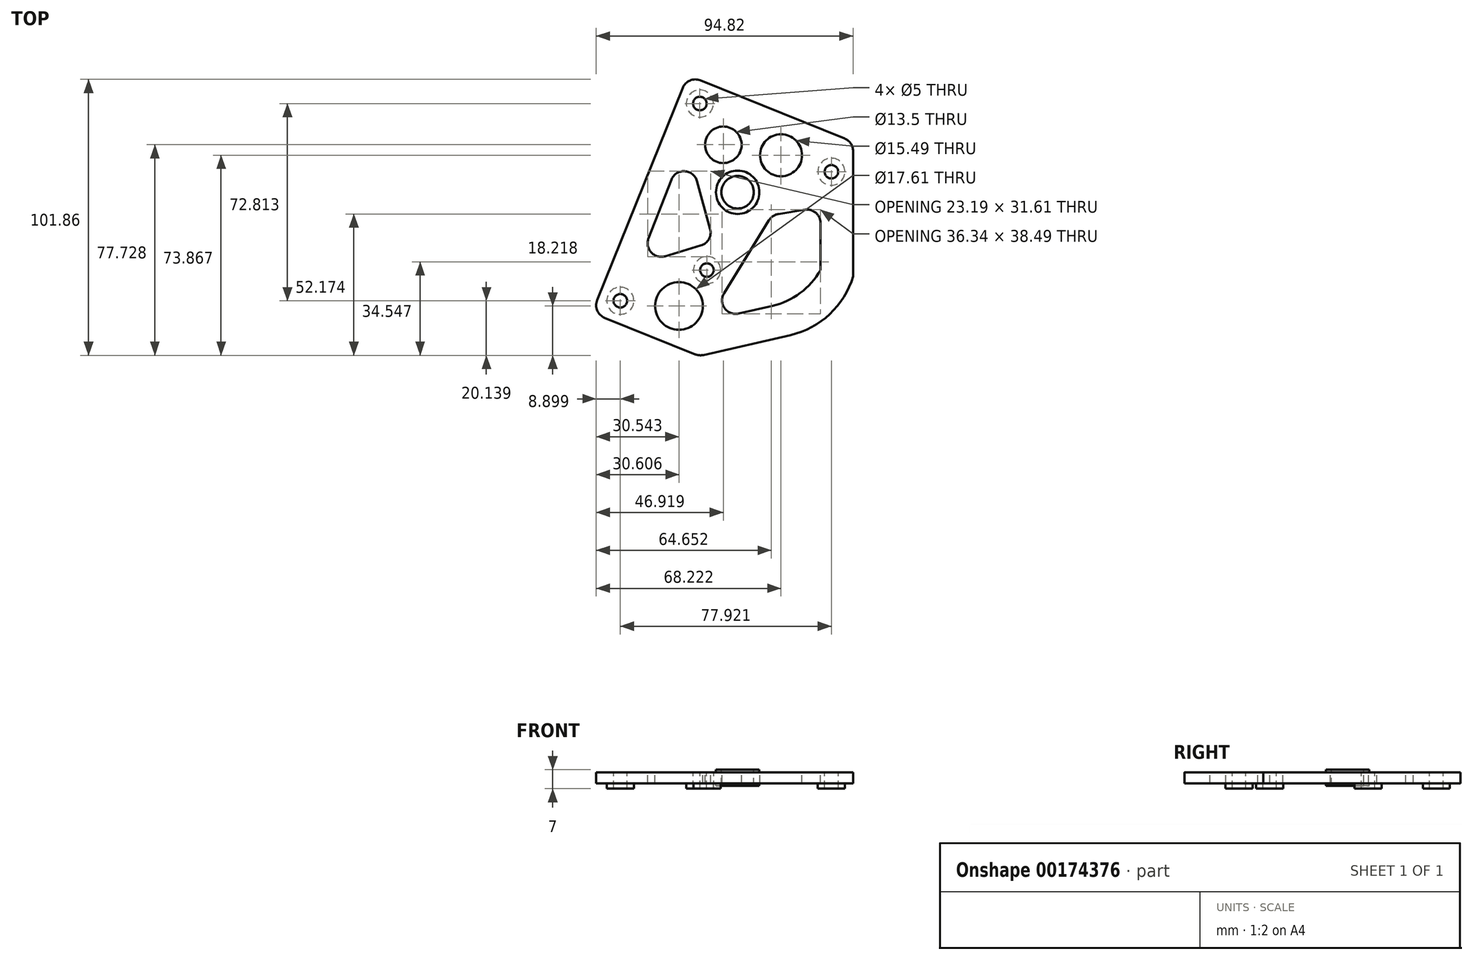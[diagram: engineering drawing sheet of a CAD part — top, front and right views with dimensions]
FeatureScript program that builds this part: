
annotation { "Feature Type Name" : "Feature", "Feature Type Description" : "" }
export const myFeature = defineFeature(function(context is Context, id is Id, definition is map)
    precondition{}
    {
        {
            var Q0;
            Q0=qCreatedBy(makeId("Top.planeOp"),FACE);
            var sketch = newSketch(context, id + "F0", { "sketchPlane" : qUnion([Q0])});
            skCircle(sketch, "E0", {"center": v(0, 0) * mm, "radius": 18.9 * mm});
            skCircle(sketch, "E1", {"center": v(0, 0) * mm, "radius": 20.4 * mm});
            skCircle(sketch, "E2", {"center": v(-30.9, 0) * mm, "radius": 2.5 * mm});
            skCircle(sketch, "E3", {"center": v(0, 0) * mm, "radius": 5.6 * mm, "construction": true});
            skCircle(sketch, "E4", {"center": v(-30.9, 0) * mm, "radius": 24.8 * mm, "construction": true});
            skCircle(sketch, "E5", {"center": v(-30.9, 0) * mm, "radius": 5.6 * mm, "construction": true});
            skCircle(sketch, "E6", {"center": v(-19.54, 28.74) * mm, "radius": 24.8 * mm, "construction": true});
            skCircle(sketch, "E7", {"center": v(-19.54, 28.74) * mm, "radius": 6 * mm});
            skLineSegment(sketch, "E8", {"start": v(-73.27, -15.75) * mm, "end": v(-37.94, 71.9) * mm});
            skLineSegment(sketch, "E9", {"start": v(-37.94, 71.9) * mm, "end": v(23.06, 47.31) * mm});
            skLineSegment(sketch, "E10", {"start": v(23.06, 47.31) * mm, "end": v(23.06, -2.33) * mm});
            skLineSegment(sketch, "E11", {"start": v(-73.27, -15.75) * mm, "end": v(-33.74, -31.69) * mm});
            skLineSegment(sketch, "E12", {"start": v(-33.74, -31.69) * mm, "end": v(0, -23.97) * mm});
            skArc(sketch, "E13", {"start": v(0, -23.97) * mm, "mid": v(14.46, -16.27) * mm, "end": v(23.06, -2.33) * mm});
            skLineSegment(sketch, "E14", {"start": v(0, 0) * mm, "end": v(9.83, 20.34) * mm, "construction": true});
            skLineSegment(sketch, "E15", {"start": v(9.83, 20.34) * mm, "end": v(-10.98, -23.06) * mm, "construction": true});
            skCircle(sketch, "E16", {"center": v(-19.54, 28.74) * mm, "radius": 8 * mm});
            skSolve(sketch);
        }
        {
            var Q0;
            Q0=makeQuery(id+"F0.imprint","IMPRINT",FACE,{"disambiguationData":[TD([[makeQuery(id+"F0.imprint","IMPRINT",EDGE,{"derivedFrom":sQuery(id+"F0.wireOp",EDGE,"E0")}),-1.0]])]});
            extrude(context, id + "F1", {"entities" : qUnion([Q0]), "oppositeDirection" : true, "depth" : 4 * mm});
        }
        {
            var Q0;
            Q0=qSketchRegion(id+"F0",true);
            extrude(context, id + "F2", {"entities" : qUnion([Q0]), "operationType" : NewBodyOperationType.ADD, "oppositeDirection" : true, "depth" : 4 * mm});
        }
        {
            var Q0;
            Q0=makeQuery(id+"F0.imprint","IMPRINT",FACE,{"disambiguationData":[TD([[makeQuery(id+"F0.imprint","IMPRINT",EDGE,{"derivedFrom":sQuery(id+"F0.wireOp",EDGE,"E0")}),1.0]])]});
            extrude(context, id + "F3", {"entities" : qUnion([Q0]), "operationType" : NewBodyOperationType.ADD, "oppositeDirection" : true, "depth" : 4 * mm});
        }
        {
            var Q0;
            Q0=makeQuery(id+"F0.imprint","IMPRINT",FACE,{"disambiguationData":[TD([[makeQuery(id+"F0.imprint","IMPRINT",EDGE,{"derivedFrom":sQuery(id+"F0.wireOp",EDGE,"E1")}),-1.0]])]});
            var sketch = newSketch(context, id + "F4", { "sketchPlane" : qUnion([Q0])});
            skCircle(sketch, "E17", {"center": v(-30.82, 0) * mm, "radius": 5 * mm});
            skCircle(sketch, "E18", {"center": v(-19.57, 28.75) * mm, "radius": 6 * mm});
            skCircle(sketch, "E19", {"center": v(15.06, 36.31) * mm, "radius": 5 * mm});
            skCircle(sketch, "E20", {"center": v(15.06, 36.31) * mm, "radius": 1.5 * mm});
            skCircle(sketch, "E21", {"center": v(-33.5, 61.5) * mm, "radius": 5 * mm});
            skCircle(sketch, "E22", {"center": v(-33.5, 61.5) * mm, "radius": 1.5 * mm});
            skCircle(sketch, "E23", {"center": v(-62.86, -11.32) * mm, "radius": 5 * mm});
            skCircle(sketch, "E24", {"center": v(-62.86, -11.32) * mm, "radius": 1.5 * mm});
            skLineSegment(sketch, "E25", {"start": v(-44.04, 33.33) * mm, "end": v(-52.43, 11.72) * mm});
            skLineSegment(sketch, "E26", {"start": v(-46.34, 5.12) * mm, "end": v(-33.12, 9.06) * mm});
            skLineSegment(sketch, "E27", {"start": v(-29.72, 15.17) * mm, "end": v(-34.55, 32.84) * mm});
            skLineSegment(sketch, "E28", {"start": v(-4.52, 20.7) * mm, "end": v(5.27, 22.28) * mm});
            skLineSegment(sketch, "E29", {"start": v(11.06, 17.34) * mm, "end": v(11.06, 0) * mm});
            skLineSegment(sketch, "E30", {"start": v(-7.98, 18.39) * mm, "end": v(-24.54, -8.55) * mm});
            skLineSegment(sketch, "E31", {"start": v(-19.16, -16.04) * mm, "end": v(-6.78, -13.2) * mm});
            skArc(sketch, "E32", {"start": v(-6.78, -13.2) * mm, "mid": v(3.52, -8.47) * mm, "end": v(11.06, 0) * mm});
            skPoint(sketch, "E33.visualSharp", {"position": v(-28.43, 10.46) * mm});
            skArc(sketch, "E33.filletArc", {"start": v(-33.12, 9.06) * mm, "mid": v(-30.17, 11.42) * mm, "end": v(-29.72, 15.17) * mm});
            skPoint(sketch, "E34.visualSharp", {"position": v(-38.55, 47.47) * mm});
            skArc(sketch, "E34.filletArc", {"start": v(-34.55, 32.84) * mm, "mid": v(-39.12, 36.52) * mm, "end": v(-44.04, 33.33) * mm});
            skPoint(sketch, "E35.visualSharp", {"position": v(-56.13, 2.2) * mm});
            skArc(sketch, "E35.filletArc", {"start": v(-52.43, 11.72) * mm, "mid": v(-51.44, 6.52) * mm, "end": v(-46.34, 5.12) * mm});
            skPoint(sketch, "E36.visualSharp", {"position": v(-30.78, -18.7) * mm});
            skArc(sketch, "E36.filletArc", {"start": v(-24.54, -8.55) * mm, "mid": v(-24.34, -14.08) * mm, "end": v(-19.16, -16.04) * mm});
            skPoint(sketch, "E37.visualSharp", {"position": v(11.06, 23.2) * mm});
            skArc(sketch, "E37.filletArc", {"start": v(11.06, 17.34) * mm, "mid": v(9.3, 21.14) * mm, "end": v(5.27, 22.28) * mm});
            skPoint(sketch, "E38.visualSharp", {"position": v(-6.78, 20.34) * mm});
            skArc(sketch, "E38.filletArc", {"start": v(-4.52, 20.7) * mm, "mid": v(-6.5, 19.92) * mm, "end": v(-7.98, 18.39) * mm});
            skCircle(sketch, "E39", {"center": v(-41.22, -13.24) * mm, "radius": 8.8 * mm});
            skCircle(sketch, "E40", {"center": v(-3.54, 42.4) * mm, "radius": 7.75 * mm});
            skCircle(sketch, "E41", {"center": v(-24.84, 46.27) * mm, "radius": 6.75 * mm});
            skSolve(sketch);
        }
        {
            var Q0;
            Q0=makeQuery(id+"F4.imprint","IMPRINT",FACE,{"disambiguationData":[TD([[makeQuery(id+"F4.imprint","IMPRINT",EDGE,{"derivedFrom":sQuery(id+"F4.wireOp",EDGE,"E17")}),1.0]])]});
            var Q1;
            Q1=sQuery(id+"F4.wireOp",EDGE,"E17");
            extrude(context, id + "F5", {"entities" : qUnion([Q0]), "operationType" : NewBodyOperationType.ADD, "surfaceEntities" : qUnion([Q1]), "oppositeDirection" : true, "depth" : 6 * mm});
        }
        {
            var Q0;
            Q0=makeQuery(id+"F4.imprint","IMPRINT",FACE,{"disambiguationData":[TD([[makeQuery(id+"F4.imprint","IMPRINT",EDGE,{"derivedFrom":sQuery(id+"F4.wireOp",EDGE,"E19")}),1.0]])]});
            var Q1;
            Q1=makeQuery(id+"F4.imprint","IMPRINT",FACE,{"disambiguationData":[TD([[makeQuery(id+"F4.imprint","IMPRINT",EDGE,{"derivedFrom":sQuery(id+"F4.wireOp",EDGE,"E21")}),1.0]])]});
            var Q2;
            Q2=makeQuery(id+"F4.imprint","IMPRINT",FACE,{"disambiguationData":[TD([[makeQuery(id+"F4.imprint","IMPRINT",EDGE,{"derivedFrom":sQuery(id+"F4.wireOp",EDGE,"E23")}),1.0]])]});
            extrude(context, id + "F6", {"entities" : qUnion([Q0, Q1, Q2]), "operationType" : NewBodyOperationType.ADD, "oppositeDirection" : true, "depth" : (31 - 25) * mm});
        }
        {
            var Q0;
            Q0=makeQuery(id+"F4.imprint","IMPRINT",FACE,{"disambiguationData":[TD([[makeQuery(id+"F4.imprint","IMPRINT",EDGE,{"derivedFrom":sQuery(id+"F4.wireOp",EDGE,"E18")}),-1.0]])]});
            extrude(context, id + "F7", {"entities" : qUnion([Q0]), "operationType" : NewBodyOperationType.ADD, "oppositeDirection" : true, "depth" : 5 * mm, "hasSecondDirection" : true, "secondDirectionOppositeDirection" : false, "secondDirectionDepth" : 1 * mm});
        }
        {
            var Q0;
            Q0=makeQuery(id+"F2.opExtrude","SWEPT_EDGE",EDGE,{"disambiguationData":[OSD([sQuery(id+"F0.wireOp",EDGE,"E8"),sQuery(id+"F0.wireOp",EDGE,"E11")])]});
            var Q1;
            Q1=makeQuery(id+"F2.opExtrude","SWEPT_EDGE",EDGE,{"disambiguationData":[OSD([sQuery(id+"F0.wireOp",EDGE,"E8"),sQuery(id+"F0.wireOp",EDGE,"E9")])]});
            var Q2;
            Q2=makeQuery(id+"F2.opExtrude","SWEPT_EDGE",EDGE,{"disambiguationData":[OSD([sQuery(id+"F0.wireOp",EDGE,"E9"),sQuery(id+"F0.wireOp",EDGE,"E10")])]});
            var Q3;
            Q3=makeQuery(id+"F2.opExtrude","SWEPT_EDGE",EDGE,{"disambiguationData":[OSD([sQuery(id+"F0.wireOp",EDGE,"E11"),sQuery(id+"F0.wireOp",EDGE,"E12")])]});
            fillet(context, id + "F8", {"entities" : qUnion([Q0, Q1, Q2, Q3]), "radius" : 5 * mm, "tangentPropagation" : true, "allowEdgeOverflow" : false});
        }
        {
            var Q0;
            Q0=sQuery(id+"F4.wireOp",VERTEX,"E22.center");
            var Q1;
            Q1=sQuery(id+"F4.wireOp",VERTEX,"E19.center");
            var Q2;
            Q2=sQuery(id+"F4.wireOp",VERTEX,"E23.center");
            var Q3;
            Q3=makeQuery(id+"F1.opExtrude","SWEPT_BODY",BODY,{"disambiguationData":[OSD([sQuery(id+"F0.wireOp",EDGE,"E0"),sQuery(id+"F0.wireOp",EDGE,"E1")])]});
            hole(context, id + "F9", {"style" : HoleStyle.SIMPLE, "endStyle" : HoleEndStyle.THROUGH, "holeDiameter" : 5 * mm, "locations" : qUnion([Q0, Q1, Q2]), "scope" : qUnion([Q3]), "isTappedThrough" : true});
        }
        {
            var Q0;
            Q0=makeQuery(id+"F4.imprint","IMPRINT",FACE,{"disambiguationData":[TD([[makeQuery(id+"F4.imprint","IMPRINT",EDGE,{"derivedFrom":sQuery(id+"F4.wireOp",EDGE,"E41")}),1.0]])]});
            var Q1;
            Q1=makeQuery(id+"F4.imprint","IMPRINT",FACE,{"disambiguationData":[TD([[makeQuery(id+"F4.imprint","IMPRINT",EDGE,{"derivedFrom":sQuery(id+"F4.wireOp",EDGE,"E25")}),1.0]])]});
            var Q2;
            {var subQ5=sQuery(id+"F4.wireOp",EDGE,"E28");Q2=makeQuery(id+"F4.imprint","IMPRINT",FACE,{"disambiguationData":[TD([[makeQuery(id+"F4.imprint","IMPRINT",EDGE,{"derivedFrom":subQ5}),-1.0]])]});}
            var Q3;
            {var subQ0=sQuery(id+"F4.wireOp",EDGE,"E32");Q3=makeQuery(id+"F4.imprint","IMPRINT",FACE,{"disambiguationData":[TD([[makeQuery(id+"F4.imprint","IMPRINT",EDGE,{"derivedFrom":subQ0}),1.0]])]});}
            var Q4;
            {var subQ0=sQuery(id+"F4.wireOp",EDGE,"E36.filletArc");Q4=makeQuery(id+"F4.imprint","IMPRINT",FACE,{"disambiguationData":[TD([[makeQuery(id+"F4.imprint","IMPRINT",EDGE,{"derivedFrom":subQ0}),1.0]])]});}
            var Q5;
            Q5=makeQuery(id+"F4.imprint","IMPRINT",FACE,{"disambiguationData":[TD([[makeQuery(id+"F4.imprint","IMPRINT",EDGE,{"derivedFrom":sQuery(id+"F4.wireOp",EDGE,"E39")}),1.0]])]});
            var Q6;
            Q6=makeQuery(id+"F4.imprint","IMPRINT",FACE,{"disambiguationData":[TD([[makeQuery(id+"F4.imprint","IMPRINT",EDGE,{"derivedFrom":sQuery(id+"F4.wireOp",EDGE,"E40")}),1.0]])]});
            extrude(context, id + "F10", {"entities" : qUnion([Q0, Q1, Q2, Q3, Q4, Q5, Q6]), "operationType" : NewBodyOperationType.REMOVE, "endBound" : BoundingType.THROUGH_ALL, "oppositeDirection" : true, "depth" : 25 * mm});
        }
    });
